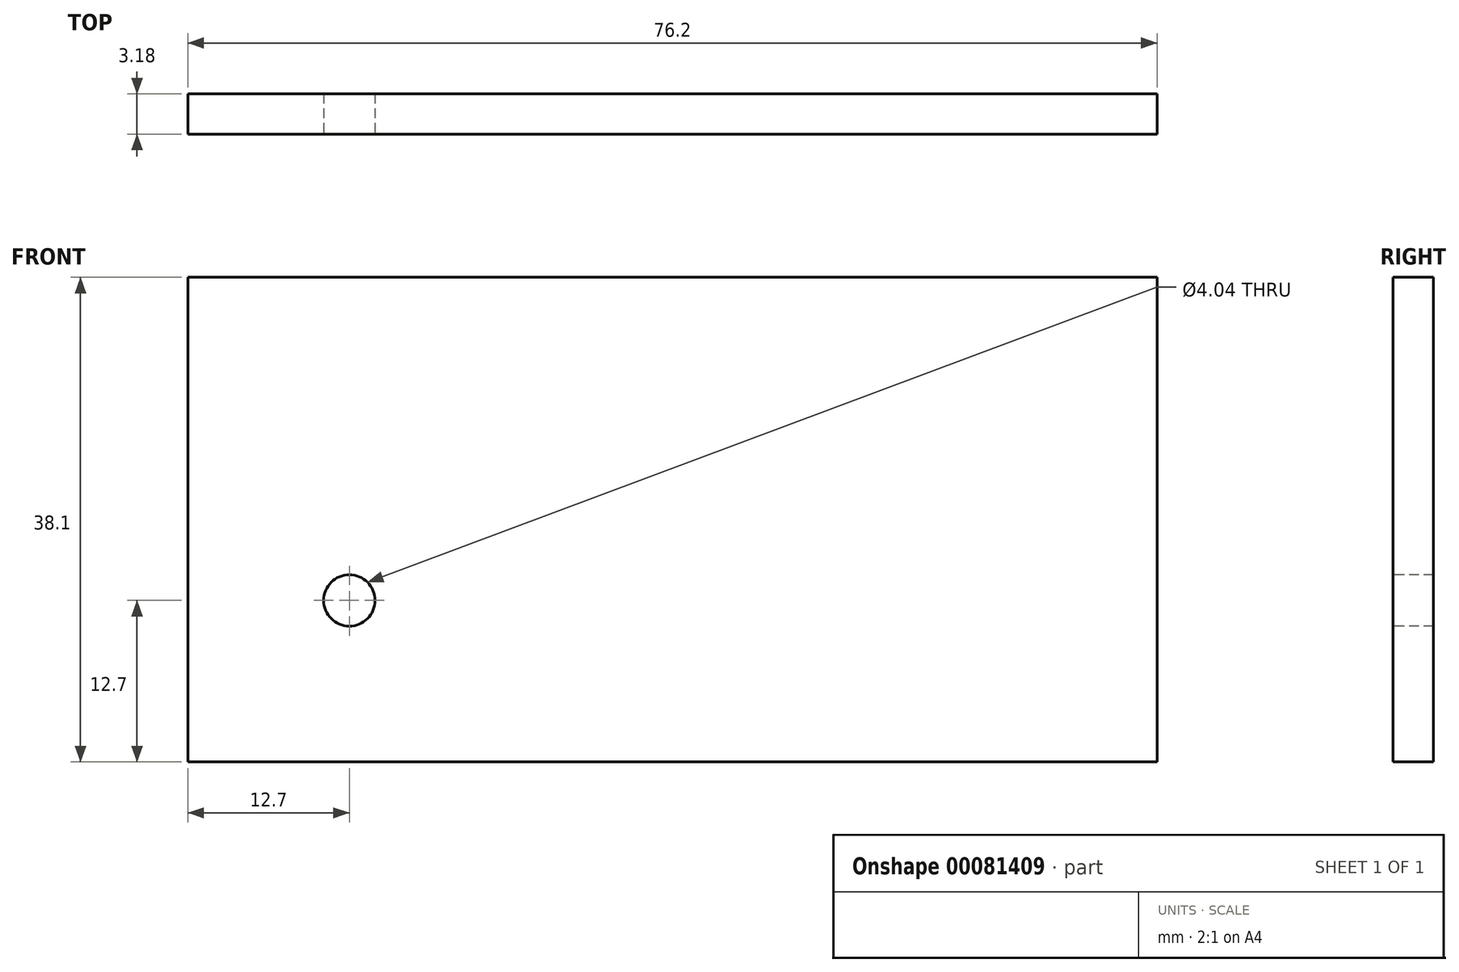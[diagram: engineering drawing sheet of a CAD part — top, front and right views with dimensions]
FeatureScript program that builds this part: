
annotation { "Feature Type Name" : "Feature", "Feature Type Description" : "" }
export const myFeature = defineFeature(function(context is Context, id is Id, definition is map)
    precondition{}
    {
        {
            var Q0;
            Q0=qCreatedBy(makeId("Front.planeOp"),FACE);
            var sketch = newSketch(context, id + "F0", { "sketchPlane" : qUnion([Q0])});
            skLineSegment(sketch, "E0.bottom", {"start": v(0, 0) * mm, "end": v(76.2, 0) * mm});
            skLineSegment(sketch, "E0.top", {"start": v(0, 38.1) * mm, "end": v(76.2, 38.1) * mm});
            skLineSegment(sketch, "E0.left", {"start": v(0, 0) * mm, "end": v(0, 38.1) * mm});
            skLineSegment(sketch, "E0.right", {"start": v(76.2, 0) * mm, "end": v(76.2, 38.1) * mm});
            skSolve(sketch);
        }
        {
            var Q0;
            Q0=makeQuery(id+"F0.imprint","IMPRINT",FACE,{"disambiguationData":[TD([[makeQuery(id+"F0.imprint","IMPRINT",EDGE,{"derivedFrom":sQuery(id+"F0.wireOp",EDGE,"E0.bottom")}),1.0]])]});
            extrude(context, id + "F1", {"entities" : qUnion([Q0]), "oppositeDirection" : true, "depth" : 3.17 * mm, "offsetDistance" : 25.4 * mm});
        }
        {
            var Q0;
            Q0=makeQuery(id+"F1.opExtrude","CAP_FACE",FACE,{"disambiguationData":[OSD([sQuery(id+"F0.wireOp",EDGE,"E0.bottom"),sQuery(id+"F0.wireOp",EDGE,"E0.top"),sQuery(id+"F0.wireOp",EDGE,"E0.left"),sQuery(id+"F0.wireOp",EDGE,"E0.right")])],"isStart":true});
            var sketch = newSketch(context, id + "F2", { "sketchPlane" : qUnion([Q0])});
            skPoint(sketch, "E1", {"position": v(12.7, 12.7) * mm});
            skSolve(sketch);
        }
        {
            var Q0;
            Q0=sQuery(id+"F2.wireOp",VERTEX,"E1");
            var Q1;
            Q1=makeQuery(id+"F1.opExtrude","SWEPT_BODY",BODY,{"disambiguationData":[OSD([sQuery(id+"F0.wireOp",EDGE,"E0.bottom"),sQuery(id+"F0.wireOp",EDGE,"E0.top"),sQuery(id+"F0.wireOp",EDGE,"E0.left"),sQuery(id+"F0.wireOp",EDGE,"E0.right")])]});
            hole(context, id + "F3", {"style" : HoleStyle.SIMPLE, "endStyle" : HoleEndStyle.THROUGH, "standardTappedOrClearance" : lookupTablePath({ "standard" : "ANSI", "engagement" : "75%", "pitch" : "32 tpi", "size" : "#10", "type" : "Tapped" }), "standardBlindInLast" : lookupTablePath({ "standard" : "ANSI", "fit" : "Free", "engagement" : "75%", "pitch" : "32 tpi", "size" : "#10", "type" : "Clearance & tapped" }), "holeDiameter" : 4.04 * mm, "majorDiameter" : 4.83 * mm, "showTappedDepth" : true, "isTappedThrough" : true, "tappedDepth" : 12.7 * mm, "tapClearance" : 3, "locations" : qUnion([Q0]), "scope" : qUnion([Q1])});
        }
    });
